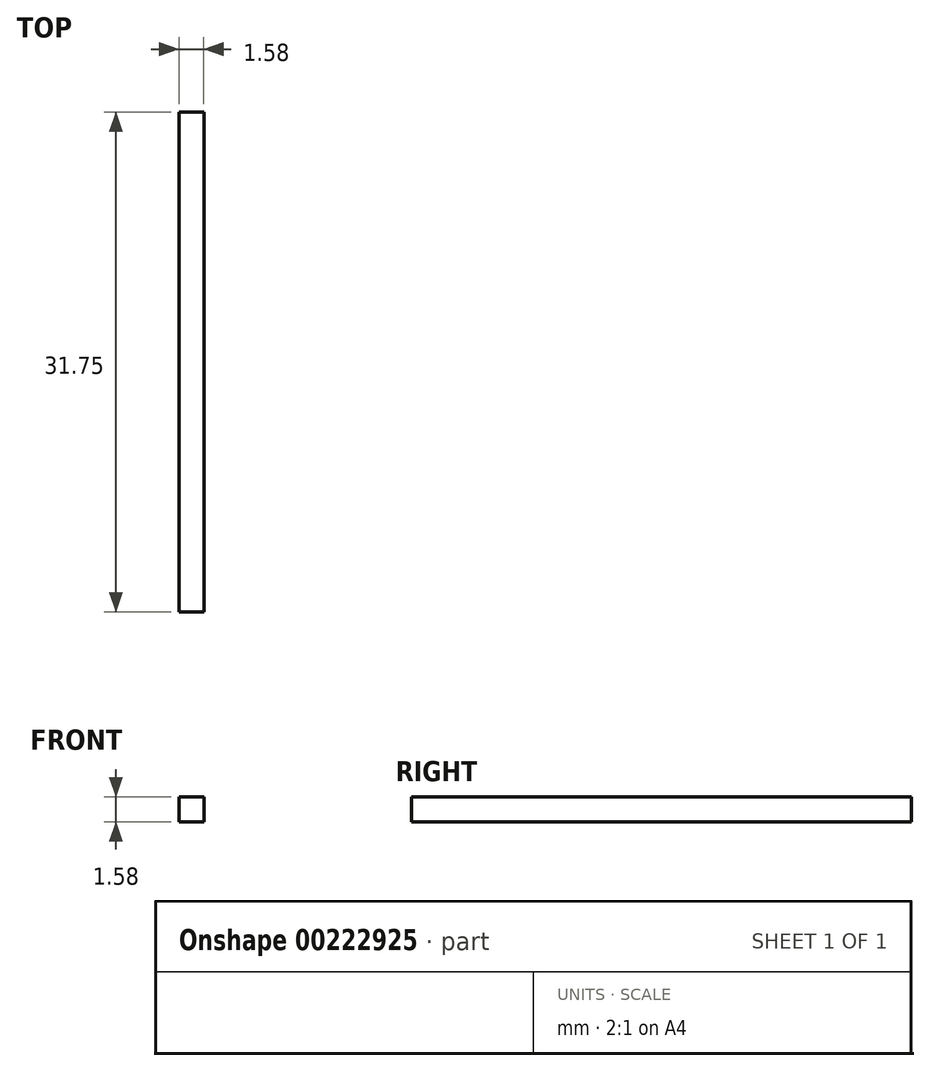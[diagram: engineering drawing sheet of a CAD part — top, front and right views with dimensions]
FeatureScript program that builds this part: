
annotation { "Feature Type Name" : "Feature", "Feature Type Description" : "" }
export const myFeature = defineFeature(function(context is Context, id is Id, definition is map)
    precondition{}
    {
        {
            var Q0;
            Q0=qCreatedBy(makeId("Front.planeOp"),FACE);
            var sketch = newSketch(context, id + "F0", { "sketchPlane" : qUnion([Q0])});
            skLineSegment(sketch, "E0.bottom", {"start": v(-2.38, 2.38) * mm, "end": v(2.38, 2.38) * mm});
            skLineSegment(sketch, "E0.top", {"start": v(-2.38, -2.38) * mm, "end": v(2.38, -2.38) * mm});
            skLineSegment(sketch, "E0.left", {"start": v(-2.38, 2.38) * mm, "end": v(-2.38, -2.38) * mm});
            skLineSegment(sketch, "E0.right", {"start": v(2.38, 2.38) * mm, "end": v(2.38, -2.38) * mm});
            skPoint(sketch, "E0.middle", {"position": v(0, 0) * mm});
            skLineSegment(sketch, "E1.bottom", {"start": v(-0.8, 2.38) * mm, "end": v(0.8, 2.38) * mm});
            skLineSegment(sketch, "E1.top", {"start": v(-0.8, -2.38) * mm, "end": v(0.8, -2.38) * mm});
            skLineSegment(sketch, "E1.left", {"start": v(-0.8, 2.38) * mm, "end": v(-0.8, -2.38) * mm});
            skLineSegment(sketch, "E1.right", {"start": v(0.8, 2.38) * mm, "end": v(0.8, -2.38) * mm});
            skLineSegment(sketch, "E2.bottom", {"start": v(-2.38, 0.8) * mm, "end": v(2.38, 0.8) * mm});
            skLineSegment(sketch, "E2.top", {"start": v(-2.38, -0.8) * mm, "end": v(2.38, -0.8) * mm});
            skLineSegment(sketch, "E2.left", {"start": v(-2.38, 0.8) * mm, "end": v(-2.38, -0.8) * mm});
            skLineSegment(sketch, "E2.right", {"start": v(2.38, 0.8) * mm, "end": v(2.38, -0.8) * mm});
            skSolve(sketch);
        }
        {
            var Q0;
            {var subQ5=sQuery(id+"F0.wireOp",EDGE,"E2.left");Q0=makeQuery(id+"F0.imprint","IMPRINT",FACE,{"disambiguationData":[TD([[makeQuery(id+"F0.imprint","IMPRINT",EDGE,{"derivedFrom":subQ5}),1.0]])]});}
            var Q1;
            {var subQ0=sQuery(id+"F0.wireOp",EDGE,"E1.bottom");Q1=makeQuery(id+"F0.imprint","IMPRINT",FACE,{"disambiguationData":[TD([[makeQuery(id+"F0.imprint","IMPRINT",EDGE,{"derivedFrom":subQ0}),-1.0]])]});}
            var Q2;
            {var subQ0=sQuery(id+"F0.wireOp",EDGE,"E2.bottom");var subQ1=sQuery(id+"F0.wireOp",EDGE,"E1.left");var subQ2=makeQuery(id+"F0.imprint","INTERSECT",VERTEX,{"derivedFrom":[subQ1,subQ0]});Q2=makeQuery(id+"F0.imprint","IMPRINT",FACE,{"disambiguationData":[TD([[makeQuery(id+"F0.imprint","IMPRINT",EDGE,{"disambiguationData":[TD([[subQ2,-1.0]])],"derivedFrom":subQ1}),1.0]])]});}
            var Q3;
            {var subQ5=sQuery(id+"F0.wireOp",EDGE,"E2.right");Q3=makeQuery(id+"F0.imprint","IMPRINT",FACE,{"disambiguationData":[TD([[makeQuery(id+"F0.imprint","IMPRINT",EDGE,{"derivedFrom":subQ5}),-1.0]])]});}
            var Q4;
            {var subQ0=sQuery(id+"F0.wireOp",EDGE,"E1.top");Q4=makeQuery(id+"F0.imprint","IMPRINT",FACE,{"disambiguationData":[TD([[makeQuery(id+"F0.imprint","IMPRINT",EDGE,{"derivedFrom":subQ0}),1.0]])]});}
            extrude(context, id + "F1", {"entities" : qUnion([Q0, Q1, Q2, Q3, Q4]), "depth" : 31.75 * mm});
        }
    });
